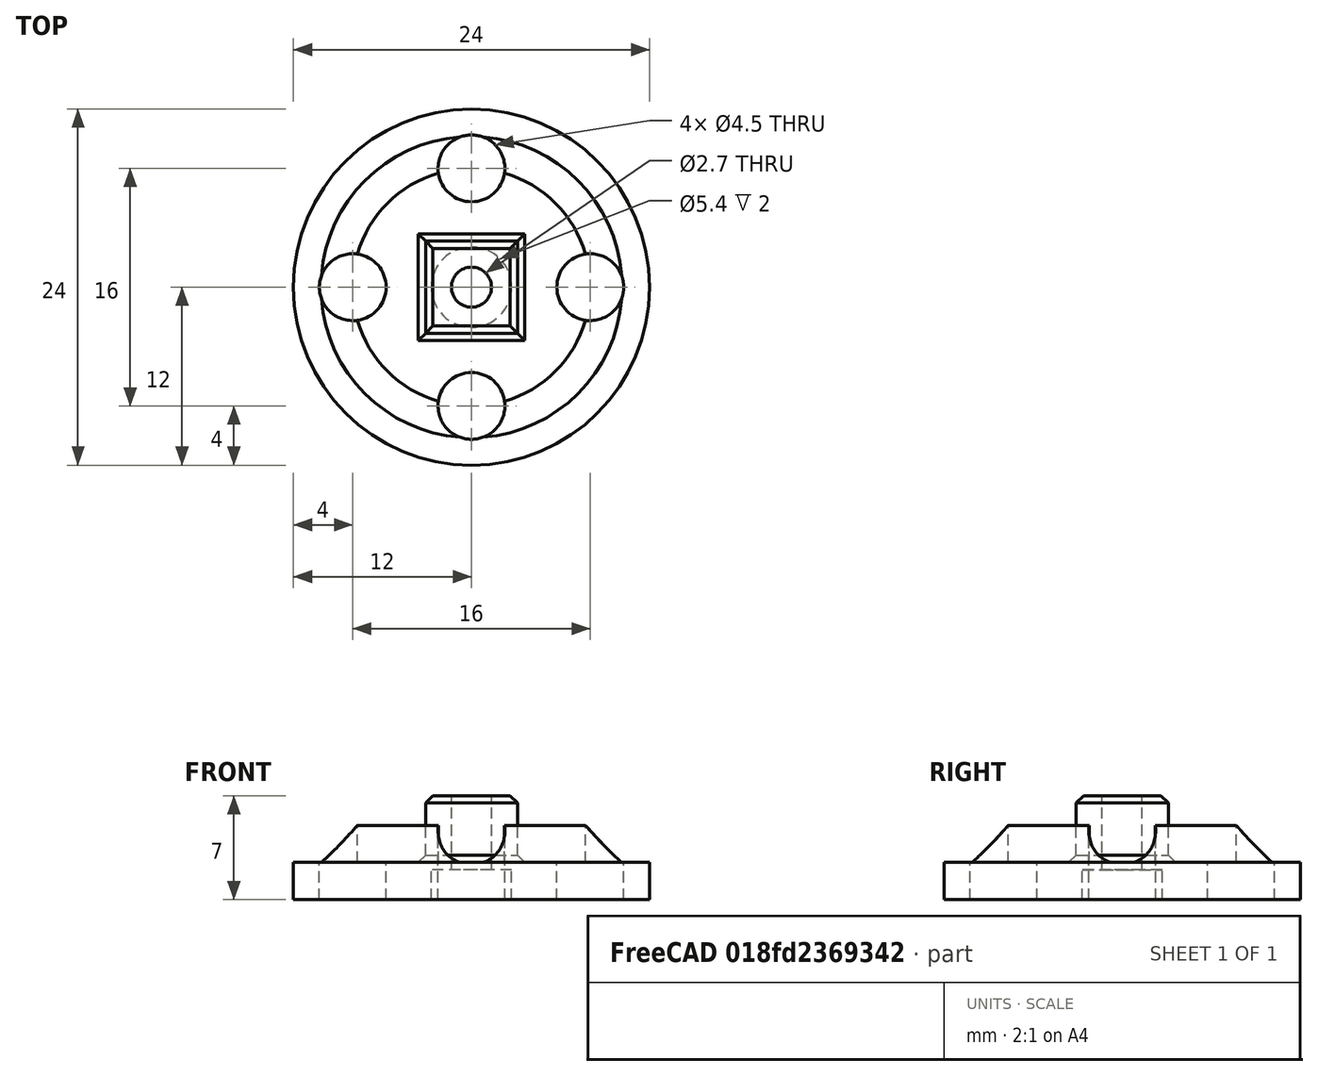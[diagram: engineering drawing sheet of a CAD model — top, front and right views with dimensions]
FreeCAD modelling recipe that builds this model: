
FCSTD DOCUMENT  (FreeCAD 0.15R4671 (Git))
Label: tendon_wheel_pwm_fingers_top
License: CC-BY 3.0
LicenseURL: http://creativecommons.org/licenses/by/3.0/
objects: Part::Cylinder×8, Part::MultiFuse×4, Part::Cut×3, Part::Chamfer×2, Part::Cone×1, Part::Box×1
note: 19 computed .brp shape members not serialized (recipe doc carries the construction recipe); baked Part::Feature solids carry a one-line shape summary decoded from their .brp

FEATURE [Part::Cylinder] Cylinder
  Angle = 360
  Height = 6
  Placement = pos=(0,0,2) rot=(0,0,1;0rad)
  Radius = 8
FEATURE [Part::Cylinder] Cylinder001
  Angle = 360
  Height = 2.5
  Placement = pos=(0,0,-0.5) rot=(0,0,1;0rad)
  Radius = 12
FEATURE [Part::Cone] Cone
  Angle = 360
  Height = 3.5
  Placement = pos=(0,0,1) rot=(0,0,1;0rad)
  Radius1 = 11
  Radius2 = 8
FEATURE [Part::Box] Box  label="Cube"
  Height = 4.5
  Length = 6.2
  Placement = pos=(-3.1,-3.1,2) rot=(0,0,1;0rad)
  Width = 6.2
FEATURE [Part::MultiFuse] Fusion
  Shapes = -> [Cone,Cylinder001]
FEATURE [Part::Cylinder] Cylinder002  label="Cylinder004"
  Angle = 360
  Height = 20
  Placement = pos=(0,0,-5) rot=(0,0,1;0rad)
  Radius = 1.35
FEATURE [Part::Cut] Cut
  Base = -> Fusion
  Tool = -> Cylinder
FEATURE [Part::MultiFuse] Fusion001
  Shapes = -> [Cut,Box]
FEATURE [Part::Cylinder] Cylinder003  label="Cylinder012"
  Angle = 360
  Height = 2
  Placement = pos=(0,0,-0.5) rot=(0,0,1;0rad)
  Radius = 2.7
FEATURE [Part::MultiFuse] Fusion002
  Shapes = -> [Cylinder003,Cylinder002]
FEATURE [Part::Cut] Cut001
  Base = -> Fusion001
  Tool = -> Fusion002
FEATURE [Part::Chamfer] Chamfer
  Base = -> Cut001
  Edges = 4 edges r=0.5: [Edge1,Edge2,Edge3,Edge4]
FEATURE [Part::Cylinder] Cylinder005  label="TopHole005"
  Angle = 360
  Height = 20
  Placement = pos=(8,0,-4) rot=(0,0,1;0rad)
  Radius = 2.25
FEATURE [Part::Cylinder] Cylinder008  label="TopHole006"
  Angle = 360
  Height = 20
  Placement = pos=(0,8,-4) rot=(0,0,1;0rad)
  Radius = 2.25
FEATURE [Part::Cylinder] Cylinder009  label="TopHole004"
  Angle = 360
  Height = 20
  Placement = pos=(-8,0,-4) rot=(0,0,1;0rad)
  Radius = 2.25
FEATURE [Part::Cylinder] Cylinder011  label="TopHole007"
  Angle = 360
  Height = 20
  Placement = pos=(0,-8,-4) rot=(0,0,1;0rad)
  Radius = 2.25
FEATURE [Part::MultiFuse] Fusion003
  Shapes = -> [Cylinder011,Cylinder008,Cylinder009,Cylinder005]
FEATURE [Part::Cut] Cut002
  Base = -> Chamfer
  Tool = -> Fusion003
FEATURE [Part::Chamfer] Chamfer001
  Base = -> Cut002
  Edges = 4 edges r=0.5: [Edge17,Edge20,Edge22,Edge23]
